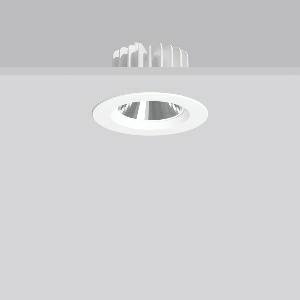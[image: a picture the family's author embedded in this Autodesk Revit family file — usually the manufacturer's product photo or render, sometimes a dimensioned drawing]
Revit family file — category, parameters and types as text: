
# Revit family: ledona_round_ip20_901791_002_7944
name_source: partatom
category: Lighting Fixtures
units: mm (PartAtom-declared; Revit-internal decimal feet)

## family parameters
Cut with Voids When Loaded = No
Host = Face
Light Source = No
Part Type = Normal
Room Calculation Point = No
Round Connector Dimension = Use Diameter
Shared = No

## types (1)
- MultiLumen 1 (1 x LED Modul 930, 1500 lm, 3000)
    Apparent Load = 12 VA
    Approval mark = CE
    CIE Flux Codes = 96 100 100 100 100
    Color Rendering = 90
    Color Temperature = 3000
    Default Elevation = 1800 mm
    Description = Series: LEDONA round
Recessed LED downlight featuring advanced technology and sophisticated design. Housing: die-cast aluminium constructed as heat sink.Bezel ring: die-cast aluminium, powder-coated. Open version. Highly polished four-segment faceted aluminium reflector with light mixing chamber. MultiLumen: Luminous flux adjustable in different steps. Best colour rendering index Ra>90. Installation without tools thanks to spring fastening system. Connected converter included in separate gearbox. With connecting cable (L 250 mm). Suitable for through-wiring with separately available accessories. Through-wiring box (5 pole) available as accessory. 
Colour: white
Diameter: 140 mm
Height: 3 mm
Cut-out diameter: 120 mm
Recess height: 79 mm
Luminaire: recess height: 79 mm
Lamp: LED
Socket: without socket
Colour temperature: 3000K
Colour rendering index (CRI): 90
System power: 12 W
Rated luminous flux: 1500 lm
Luminous efficiency: 125 lm/W
System power 2: 16 W
Rated luminous flux 2: 1950 lm
Luminous efficiency 2: 122 lm/W
System power 3: 19 W
Rated luminous flux 3: 2400 lm
Luminous efficiency 3: 126 lm/W
System power 4: 25 W
Rated luminous flux 4: 3000 lm
Luminous efficiency 4: 120 lm/W
Control gear: Regulated power supply
Protection class: II
Type of protection: IP 20
    Height = 0 mm  [stored 0 ft]
    Lamp = 1 x LED Modul 930
    Lamp Light Flux = 1500 lm
    Lamp count = 1
    Length = 140 mm  [stored 0.459318 ft]
    Lifetime = 50000 h
    Luminous efficacy = 125 lm/W
    Manufacturer = RZB
    ModVariant = No
    Model = 901791.002
    Mounting Place = Ceiling
    Mounting Type = Recessed
    Number of Poles = 1
    OnlyDefault = Yes
    Power Factor = 1
    Product Name = LEDONA round IP20
    Product group = Recessed downlights
    ProductGroupID = 402
    Protection Class = Protection class II
    Protection Degree = IP 20
    RLX_Detail_Level = 1
    RLX_Emergency_Light_Flux = 0 lm
    RLX_Emergency_Type = 0
    RLX_Emergency_Type_DB = No
    RlxData = <blob elided: 34973 chars, md5=e120aeec>
    Socket = socket
    Standby Power = 0 W
    System Light Flux = 1500 lm
    System Power = 12 W
    Type Comments = MultiLumen 1
    Type Image = 901383.002.jpg
    URL = http://relux.com
    VarID = multilumen_1
    Voltage = 230 V
    Voltage Range = 220-240 V
    Weight = 0.00 kg
    Width = 0 mm  [stored 0 ft]

note: [stored X ft] marks values corroborated as IEEE doubles in the binary element streams (Revit-internal decimal feet)

## geometry (parser evidence)
native form markers: Blend x4, Sweep x9
no freeform markers — native parametric forms only
